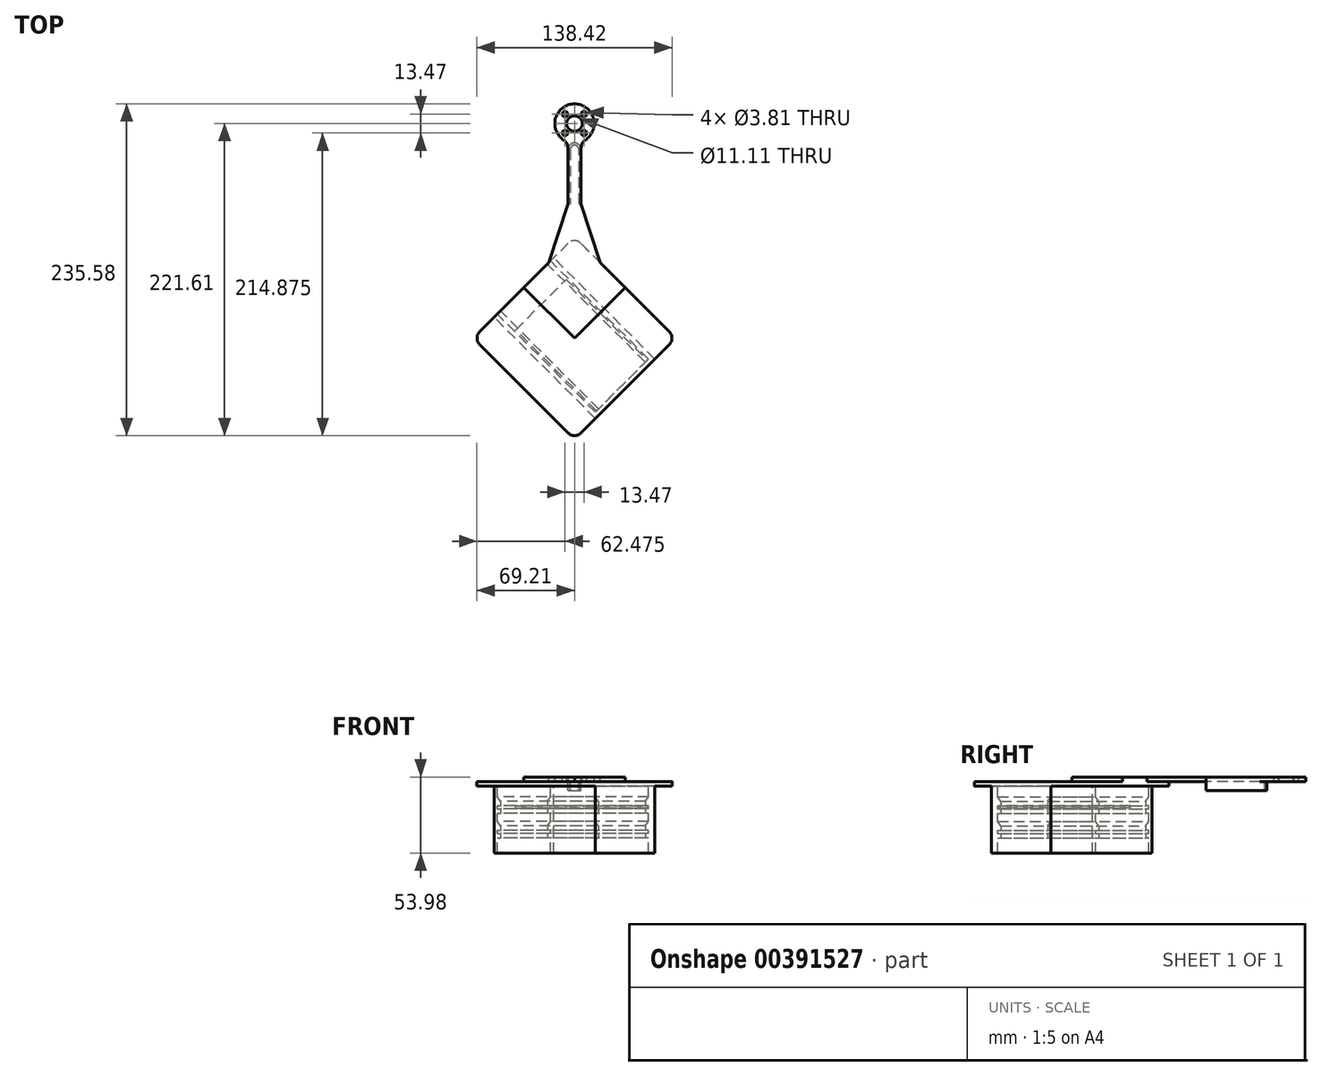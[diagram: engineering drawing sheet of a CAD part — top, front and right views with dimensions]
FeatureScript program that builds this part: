
annotation { "Feature Type Name" : "Feature", "Feature Type Description" : "" }
export const myFeature = defineFeature(function(context is Context, id is Id, definition is map)
    precondition{}
    {
        {
            var Q0;
            Q0=qCreatedBy(makeId("Top.planeOp"),FACE);
            var sketch = newSketch(context, id + "F0", { "sketchPlane" : qUnion([Q0])});
            skArc(sketch, "E0", {"start": v(4.76, 139.27) * mm, "mid": v(0, 166.37) * mm, "end": v(-4.76, 139.27) * mm});
            skCircle(sketch, "E1", {"center": v(0, 152.4) * mm, "radius": 8.06 * mm, "construction": true});
            skCircle(sketch, "E2", {"center": v(0, 152.4) * mm, "radius": 5.56 * mm});
            skCircle(sketch, "E3", {"center": v(0, 152.4) * mm, "radius": 9.53 * mm, "construction": true});
            skLineSegment(sketch, "E4", {"start": v(0, 152.4) * mm, "end": v(-9.52, 152.4) * mm, "construction": true});
            skLineSegment(sketch, "E5", {"start": v(0, 152.4) * mm, "end": v(-6.74, 159.14) * mm, "construction": true});
            skCircle(sketch, "E6", {"center": v(-6.74, 159.14) * mm, "radius": 1.9 * mm});
            skLineSegment(sketch, "E7", {"start": v(0, 152.4) * mm, "end": v(6.74, 159.14) * mm, "construction": true});
            skCircle(sketch, "E8", {"center": v(6.74, 159.14) * mm, "radius": 1.9 * mm});
            skCircle(sketch, "E9", {"center": v(6.74, 145.66) * mm, "radius": 1.9 * mm});
            skCircle(sketch, "E10", {"center": v(-6.74, 145.66) * mm, "radius": 1.9 * mm});
            skLineSegment(sketch, "E11.top", {"start": v(-18.32, 53.52) * mm, "end": v(-35.92, 35.92) * mm});
            skLineSegment(sketch, "E11.left", {"start": v(35.92, 35.92) * mm, "end": v(18.32, 53.52) * mm});
            skPoint(sketch, "E11.middle", {"position": v(0, 0) * mm});
            skLineSegment(sketch, "E12", {"start": v(0, 152.4) * mm, "end": v(0, 71.84) * mm, "construction": true});
            skLineSegment(sketch, "E13", {"start": v(-4.76, 139.27) * mm, "end": v(-4.76, 95.25) * mm});
            skLineSegment(sketch, "E14", {"start": v(-4.76, 95.25) * mm, "end": v(-18.32, 53.52) * mm});
            skLineSegment(sketch, "E15.MirrorCS", {"start": v(4.76, 95.25) * mm, "end": v(18.32, 53.52) * mm});
            skLineSegment(sketch, "E16.MirrorCS", {"start": v(4.76, 139.27) * mm, "end": v(4.76, 95.25) * mm});
            skLineSegment(sketch, "E17", {"start": v(0, 0) * mm, "end": v(-35.92, 35.92) * mm});
            skLineSegment(sketch, "E18", {"start": v(0, 0) * mm, "end": v(35.92, 35.92) * mm});
            skLineSegment(sketch, "E19", {"start": v(0, -71.84) * mm, "end": v(-71.84, 0) * mm, "construction": true});
            skLineSegment(sketch, "E20", {"start": v(-71.84, 0) * mm, "end": v(0, 71.84) * mm, "construction": true});
            skLineSegment(sketch, "E21", {"start": v(0, 71.84) * mm, "end": v(71.84, 0) * mm, "construction": true});
            skLineSegment(sketch, "E22", {"start": v(71.84, 0) * mm, "end": v(0, -71.84) * mm, "construction": true});
            skLineSegment(sketch, "E23", {"start": v(-35.92, -35.92) * mm, "end": v(35.92, 35.92) * mm, "construction": true});
            skLineSegment(sketch, "E24", {"start": v(35.92, -35.92) * mm, "end": v(-35.92, 35.92) * mm, "construction": true});
            skSolve(sketch);
        }
        {
            var Q0;
            Q0 = qSketchRegion(id + "F0", true);
            extrude(context, id + "F1", {"entities" : qUnion([Q0]), "oppositeDirection" : true, "depth" : 3.17 * mm});
        }
        {
            var Q0;
            Q0=makeQuery(id+"F1.opExtrude","CAP_FACE",FACE,{"disambiguationData":[OSD([sQuery(id+"F0.wireOp",EDGE,"E0"),sQuery(id+"F0.wireOp",EDGE,"E2"),sQuery(id+"F0.wireOp",EDGE,"E6"),sQuery(id+"F0.wireOp",EDGE,"E8"),sQuery(id+"F0.wireOp",EDGE,"E9"),sQuery(id+"F0.wireOp",EDGE,"E10"),sQuery(id+"F0.wireOp",EDGE,"E11.bottom"),sQuery(id+"F0.wireOp",EDGE,"E11.top"),sQuery(id+"F0.wireOp",EDGE,"E11.left"),sQuery(id+"F0.wireOp",EDGE,"E11.right"),sQuery(id+"F0.wireOp",EDGE,"E13"),sQuery(id+"F0.wireOp",EDGE,"E14"),sQuery(id+"F0.wireOp",EDGE,"E15.MirrorCS"),sQuery(id+"F0.wireOp",EDGE,"E16.MirrorCS"),sQuery(id+"F0.wireOp",EDGE,"a6862504-0e44-4ac9-902f-c619737a087e.1.1"),sQuery(id+"F0.wireOp",EDGE,"a6862504-0e44-4ac9-902f-c619737a087e.1.3"),sQuery(id+"F0.wireOp",EDGE,"a6862504-0e44-4ac9-902f-c619737a087e.1.4"),sQuery(id+"F0.wireOp",EDGE,"a6862504-0e44-4ac9-902f-c619737a087e.1.5"),sQuery(id+"F0.wireOp",EDGE,"a6862504-0e44-4ac9-902f-c619737a087e.1.7"),sQuery(id+"F0.wireOp",EDGE,"a6862504-0e44-4ac9-902f-c619737a087e.1.9"),sQuery(id+"F0.wireOp",EDGE,"a6862504-0e44-4ac9-902f-c619737a087e.1.11"),sQuery(id+"F0.wireOp",EDGE,"a6862504-0e44-4ac9-902f-c619737a087e.1.12"),sQuery(id+"F0.wireOp",EDGE,"a6862504-0e44-4ac9-902f-c619737a087e.1.13"),sQuery(id+"F0.wireOp",EDGE,"a6862504-0e44-4ac9-902f-c619737a087e.1.14"),sQuery(id+"F0.wireOp",EDGE,"a6862504-0e44-4ac9-902f-c619737a087e.2.1"),sQuery(id+"F0.wireOp",EDGE,"a6862504-0e44-4ac9-902f-c619737a087e.2.3"),sQuery(id+"F0.wireOp",EDGE,"a6862504-0e44-4ac9-902f-c619737a087e.2.4"),sQuery(id+"F0.wireOp",EDGE,"a6862504-0e44-4ac9-902f-c619737a087e.2.5"),sQuery(id+"F0.wireOp",EDGE,"a6862504-0e44-4ac9-902f-c619737a087e.2.7"),sQuery(id+"F0.wireOp",EDGE,"a6862504-0e44-4ac9-902f-c619737a087e.2.9"),sQuery(id+"F0.wireOp",EDGE,"a6862504-0e44-4ac9-902f-c619737a087e.2.11"),sQuery(id+"F0.wireOp",EDGE,"a6862504-0e44-4ac9-902f-c619737a087e.2.12"),sQuery(id+"F0.wireOp",EDGE,"a6862504-0e44-4ac9-902f-c619737a087e.2.13"),sQuery(id+"F0.wireOp",EDGE,"a6862504-0e44-4ac9-902f-c619737a087e.2.14"),sQuery(id+"F0.wireOp",EDGE,"a6862504-0e44-4ac9-902f-c619737a087e.3.1"),sQuery(id+"F0.wireOp",EDGE,"a6862504-0e44-4ac9-902f-c619737a087e.3.3"),sQuery(id+"F0.wireOp",EDGE,"a6862504-0e44-4ac9-902f-c619737a087e.3.4"),sQuery(id+"F0.wireOp",EDGE,"a6862504-0e44-4ac9-902f-c619737a087e.3.5"),sQuery(id+"F0.wireOp",EDGE,"a6862504-0e44-4ac9-902f-c619737a087e.3.7"),sQuery(id+"F0.wireOp",EDGE,"a6862504-0e44-4ac9-902f-c619737a087e.3.9"),sQuery(id+"F0.wireOp",EDGE,"a6862504-0e44-4ac9-902f-c619737a087e.3.11"),sQuery(id+"F0.wireOp",EDGE,"a6862504-0e44-4ac9-902f-c619737a087e.3.12"),sQuery(id+"F0.wireOp",EDGE,"a6862504-0e44-4ac9-902f-c619737a087e.3.13"),sQuery(id+"F0.wireOp",EDGE,"a6862504-0e44-4ac9-902f-c619737a087e.3.14")])],"isStart":false});
            var sketch = newSketch(context, id + "F2", { "sketchPlane" : qUnion([Q0])});
            skLineSegment(sketch, "E25", {"start": v(14.82, 57.02) * mm, "end": v(-57.02, -14.82) * mm});
            skLineSegment(sketch, "E26", {"start": v(-57.02, -14.82) * mm, "end": v(-54.78, -17.06) * mm});
            skLineSegment(sketch, "E27", {"start": v(-54.78, -17.06) * mm, "end": v(14.82, 52.53) * mm});
            skLineSegment(sketch, "E28", {"start": v(17.06, 54.78) * mm, "end": v(14.82, 57.02) * mm});
            skLineSegment(sketch, "E29", {"start": v(0, 0) * mm, "end": v(-35.92, 35.92) * mm, "construction": true});
            skLineSegment(sketch, "E30", {"start": v(0, 0) * mm, "end": v(35.92, 35.92) * mm, "construction": true});
            skLineSegment(sketch, "E31", {"start": v(35.92, 35.92) * mm, "end": v(-35.92, -35.92) * mm, "construction": true});
            skLineSegment(sketch, "E32.MirrorCS", {"start": v(54.78, 17.06) * mm, "end": v(57.02, 14.82) * mm});
            skLineSegment(sketch, "E33.MirrorCS", {"start": v(-14.82, -57.02) * mm, "end": v(-17.06, -54.78) * mm});
            skLineSegment(sketch, "E34.MirrorCS", {"start": v(57.02, 14.82) * mm, "end": v(-14.82, -57.02) * mm});
            skLineSegment(sketch, "E35.MirrorCS", {"start": v(-17.06, -54.78) * mm, "end": v(52.53, 14.82) * mm});
            skLineSegment(sketch, "E36", {"start": v(17.06, 54.78) * mm, "end": v(54.78, 17.06) * mm});
            skLineSegment(sketch, "E37", {"start": v(14.82, 52.53) * mm, "end": v(52.53, 14.82) * mm});
            skSolve(sketch);
        }
        {
            var Q0;
            Q0 = qSketchRegion(id + "F2", true);
            extrude(context, id + "F3", {"entities" : qUnion([Q0]), "depth" : 50.8 * mm});
        }
        {
            var Q0;
            Q0=makeQuery(id+"F3.opExtrude","SWEPT_FACE",FACE,{"disambiguationData":[OSD([sQuery(id+"F2.wireOp",EDGE,"E33.MirrorCS")])]});
            var sketch = newSketch(context, id + "F4", { "sketchPlane" : qUnion([Q0])});
            skLineSegment(sketch, "E38.top", {"start": v(-26.67, -20.32) * mm, "end": v(-23.5, -20.32) * mm});
            skLineSegment(sketch, "E38.left", {"start": v(-26.67, -19.05) * mm, "end": v(-26.67, -20.32) * mm});
            skLineSegment(sketch, "E38.right", {"start": v(-23.5, -17.14) * mm, "end": v(-23.5, -20.32) * mm});
            skLineSegment(sketch, "E39.bottom", {"start": v(-26.67, -22.48) * mm, "end": v(-23.5, -22.48) * mm});
            skLineSegment(sketch, "E39.top", {"start": v(-26.67, -25.65) * mm, "end": v(-23.5, -25.65) * mm});
            skLineSegment(sketch, "E39.left", {"start": v(-26.67, -22.48) * mm, "end": v(-26.67, -25.65) * mm});
            skLineSegment(sketch, "E39.right", {"start": v(-23.5, -22.48) * mm, "end": v(-23.5, -25.65) * mm});
            skLineSegment(sketch, "E40", {"start": v(0, 0) * mm, "end": v(0, -54) * mm, "construction": true});
            skLineSegment(sketch, "E41.MirrorCS", {"start": v(26.67, -22.48) * mm, "end": v(26.67, -25.65) * mm});
            skLineSegment(sketch, "E42.MirrorCS", {"start": v(26.67, -25.65) * mm, "end": v(23.5, -25.65) * mm});
            skLineSegment(sketch, "E43.MirrorCS", {"start": v(26.67, -22.48) * mm, "end": v(23.5, -22.48) * mm});
            skLineSegment(sketch, "E44.MirrorCS", {"start": v(23.5, -22.48) * mm, "end": v(23.5, -25.65) * mm});
            skLineSegment(sketch, "E45.MirrorCS", {"start": v(23.5, -17.14) * mm, "end": v(23.5, -20.32) * mm});
            skLineSegment(sketch, "E46.MirrorCS", {"start": v(26.67, -20.32) * mm, "end": v(23.5, -20.32) * mm});
            skLineSegment(sketch, "E47.MirrorCS", {"start": v(26.67, -19.05) * mm, "end": v(26.67, -20.32) * mm});
            skLineSegment(sketch, "E48", {"start": v(-23.5, -17.15) * mm, "end": v(-26.67, -13.97) * mm});
            skLineSegment(sketch, "E49", {"start": v(23.5, -17.15) * mm, "end": v(26.67, -13.97) * mm});
            skLineSegment(sketch, "E50", {"start": v(-26.67, -13.97) * mm, "end": v(-26.67, -19.05) * mm});
            skLineSegment(sketch, "E51", {"start": v(26.67, -13.97) * mm, "end": v(26.67, -19.05) * mm});
            skLineSegment(sketch, "E52.0.1.0", {"start": v(-26.67, -39.94) * mm, "end": v(-23.5, -39.94) * mm});
            skLineSegment(sketch, "E52.0.1.1", {"start": v(-26.67, -36.51) * mm, "end": v(-26.67, -37.78) * mm});
            skLineSegment(sketch, "E52.0.1.2", {"start": v(-26.67, -37.78) * mm, "end": v(-23.5, -37.78) * mm});
            skLineSegment(sketch, "E52.0.1.3", {"start": v(-23.5, -34.6) * mm, "end": v(-23.5, -37.78) * mm});
            skLineSegment(sketch, "E52.0.1.4", {"start": v(-23.5, -34.6) * mm, "end": v(-26.67, -31.43) * mm});
            skLineSegment(sketch, "E52.0.1.5", {"start": v(26.67, -36.51) * mm, "end": v(26.67, -37.78) * mm});
            skLineSegment(sketch, "E52.0.1.6", {"start": v(-26.67, -43.12) * mm, "end": v(-23.5, -43.12) * mm});
            skLineSegment(sketch, "E52.0.1.7", {"start": v(-26.67, -39.94) * mm, "end": v(-26.67, -43.12) * mm});
            skLineSegment(sketch, "E52.0.1.8", {"start": v(26.67, -31.43) * mm, "end": v(26.67, -36.51) * mm});
            skLineSegment(sketch, "E52.0.1.9", {"start": v(23.5, -34.6) * mm, "end": v(26.67, -31.43) * mm});
            skLineSegment(sketch, "E52.0.1.10", {"start": v(26.67, -37.78) * mm, "end": v(23.5, -37.78) * mm});
            skLineSegment(sketch, "E52.0.1.11", {"start": v(-23.5, -39.94) * mm, "end": v(-23.5, -43.12) * mm});
            skLineSegment(sketch, "E52.0.1.12", {"start": v(26.67, -39.94) * mm, "end": v(26.67, -43.12) * mm});
            skLineSegment(sketch, "E52.0.1.13", {"start": v(26.67, -43.12) * mm, "end": v(23.5, -43.12) * mm});
            skLineSegment(sketch, "E52.0.1.14", {"start": v(26.67, -39.94) * mm, "end": v(23.5, -39.94) * mm});
            skLineSegment(sketch, "E52.0.1.15", {"start": v(23.5, -39.94) * mm, "end": v(23.5, -43.12) * mm});
            skLineSegment(sketch, "E52.0.1.16", {"start": v(23.5, -34.6) * mm, "end": v(23.5, -37.78) * mm});
            skLineSegment(sketch, "E52.0.1.17", {"start": v(-26.67, -31.43) * mm, "end": v(-26.67, -36.51) * mm});
            skLineSegment(sketch, "E52.direction1", {"start": v(-26.67, -25.65) * mm, "end": v(-1.27, -25.65) * mm, "construction": true});
            skLineSegment(sketch, "E52.direction2", {"start": v(-26.67, -25.65) * mm, "end": v(-26.67, -43.12) * mm, "construction": true});
            skSolve(sketch);
        }
        {
            var Q0;
            Q0 = qSketchRegion(id + "F4", true);
            var Q1;
            Q1=makeQuery(id+"F3.opExtrude","SWEPT_FACE",FACE,{"disambiguationData":[OSD([sQuery(id+"F2.wireOp",EDGE,"E37")])]});
            extrude(context, id + "F5", {"entities" : qUnion([Q0]), "operationType" : NewBodyOperationType.ADD, "endBound" : BoundingType.UP_TO_SURFACE, "oppositeDirection" : true, "endBoundEntityFace" : qUnion([Q1]), "depth" : 25.4 * mm});
        }
        {
            var Q0;
            Q0=makeQuery(id+"F5.opExtrude","SWEPT_FACE",FACE,{"disambiguationData":[OSD([sQuery(id+"F4.wireOp",EDGE,"E38.top")])]});
            var sketch = newSketch(context, id + "F6", { "sketchPlane" : qUnion([Q0])});
            skLineSegment(sketch, "E53", {"start": v(15.72, 51.64) * mm, "end": v(-41.76, -5.84) * mm});
            skLineSegment(sketch, "E54", {"start": v(-41.76, -5.84) * mm, "end": v(-5.84, -41.76) * mm});
            skLineSegment(sketch, "E55", {"start": v(-5.84, -41.76) * mm, "end": v(51.64, 15.72) * mm});
            skLineSegment(sketch, "E56", {"start": v(51.64, 15.72) * mm, "end": v(15.72, 51.64) * mm});
            skLineSegment(sketch, "E57", {"start": v(33.68, 33.68) * mm, "end": v(-23.8, -23.8) * mm, "construction": true});
            skLineSegment(sketch, "E58", {"start": v(-13.02, 22.9) * mm, "end": v(22.9, -13.02) * mm, "construction": true});
            skPoint(sketch, "E59", {"position": v(4.94, 4.94) * mm});
            skLineSegment(sketch, "E60", {"start": v(0, 0) * mm, "end": v(90.54, 90.54) * mm, "construction": true});
            skSolve(sketch);
        }
        {
            var Q0;
            Q0 = qSketchRegion(id + "F6", true);
            extrude(context, id + "F7", {"entities" : qUnion([Q0]), "depth" : 1.78 * mm});
        }
        {
            var Q0;
            Q0=makeQuery(id+"F1.opExtrude","CAP_FACE",FACE,{"disambiguationData":[OSD([sQuery(id+"F0.wireOp",EDGE,"E0"),sQuery(id+"F0.wireOp",EDGE,"E2"),sQuery(id+"F0.wireOp",EDGE,"E6"),sQuery(id+"F0.wireOp",EDGE,"E8"),sQuery(id+"F0.wireOp",EDGE,"E9"),sQuery(id+"F0.wireOp",EDGE,"E10"),sQuery(id+"F0.wireOp",EDGE,"E11.bottom"),sQuery(id+"F0.wireOp",EDGE,"E11.top"),sQuery(id+"F0.wireOp",EDGE,"E11.left"),sQuery(id+"F0.wireOp",EDGE,"E11.right"),sQuery(id+"F0.wireOp",EDGE,"E13"),sQuery(id+"F0.wireOp",EDGE,"E14"),sQuery(id+"F0.wireOp",EDGE,"E15.MirrorCS"),sQuery(id+"F0.wireOp",EDGE,"E16.MirrorCS"),sQuery(id+"F0.wireOp",EDGE,"a6862504-0e44-4ac9-902f-c619737a087e.1.1"),sQuery(id+"F0.wireOp",EDGE,"a6862504-0e44-4ac9-902f-c619737a087e.1.3"),sQuery(id+"F0.wireOp",EDGE,"a6862504-0e44-4ac9-902f-c619737a087e.1.4"),sQuery(id+"F0.wireOp",EDGE,"a6862504-0e44-4ac9-902f-c619737a087e.1.5"),sQuery(id+"F0.wireOp",EDGE,"a6862504-0e44-4ac9-902f-c619737a087e.1.7"),sQuery(id+"F0.wireOp",EDGE,"a6862504-0e44-4ac9-902f-c619737a087e.1.9"),sQuery(id+"F0.wireOp",EDGE,"a6862504-0e44-4ac9-902f-c619737a087e.1.11"),sQuery(id+"F0.wireOp",EDGE,"a6862504-0e44-4ac9-902f-c619737a087e.1.12"),sQuery(id+"F0.wireOp",EDGE,"a6862504-0e44-4ac9-902f-c619737a087e.1.13"),sQuery(id+"F0.wireOp",EDGE,"a6862504-0e44-4ac9-902f-c619737a087e.1.14"),sQuery(id+"F0.wireOp",EDGE,"a6862504-0e44-4ac9-902f-c619737a087e.2.1"),sQuery(id+"F0.wireOp",EDGE,"a6862504-0e44-4ac9-902f-c619737a087e.2.3"),sQuery(id+"F0.wireOp",EDGE,"a6862504-0e44-4ac9-902f-c619737a087e.2.4"),sQuery(id+"F0.wireOp",EDGE,"a6862504-0e44-4ac9-902f-c619737a087e.2.5"),sQuery(id+"F0.wireOp",EDGE,"a6862504-0e44-4ac9-902f-c619737a087e.2.7"),sQuery(id+"F0.wireOp",EDGE,"a6862504-0e44-4ac9-902f-c619737a087e.2.9"),sQuery(id+"F0.wireOp",EDGE,"a6862504-0e44-4ac9-902f-c619737a087e.2.11"),sQuery(id+"F0.wireOp",EDGE,"a6862504-0e44-4ac9-902f-c619737a087e.2.12"),sQuery(id+"F0.wireOp",EDGE,"a6862504-0e44-4ac9-902f-c619737a087e.2.13"),sQuery(id+"F0.wireOp",EDGE,"a6862504-0e44-4ac9-902f-c619737a087e.2.14"),sQuery(id+"F0.wireOp",EDGE,"a6862504-0e44-4ac9-902f-c619737a087e.3.1"),sQuery(id+"F0.wireOp",EDGE,"a6862504-0e44-4ac9-902f-c619737a087e.3.3"),sQuery(id+"F0.wireOp",EDGE,"a6862504-0e44-4ac9-902f-c619737a087e.3.4"),sQuery(id+"F0.wireOp",EDGE,"a6862504-0e44-4ac9-902f-c619737a087e.3.5"),sQuery(id+"F0.wireOp",EDGE,"a6862504-0e44-4ac9-902f-c619737a087e.3.7"),sQuery(id+"F0.wireOp",EDGE,"a6862504-0e44-4ac9-902f-c619737a087e.3.9"),sQuery(id+"F0.wireOp",EDGE,"a6862504-0e44-4ac9-902f-c619737a087e.3.11"),sQuery(id+"F0.wireOp",EDGE,"a6862504-0e44-4ac9-902f-c619737a087e.3.12"),sQuery(id+"F0.wireOp",EDGE,"a6862504-0e44-4ac9-902f-c619737a087e.3.13"),sQuery(id+"F0.wireOp",EDGE,"a6862504-0e44-4ac9-902f-c619737a087e.3.14")])],"isStart":false});
            var sketch = newSketch(context, id + "F8", { "sketchPlane" : qUnion([Q0])});
            skLineSegment(sketch, "E61", {"start": v(0, 71.84) * mm, "end": v(71.84, 0) * mm});
            skLineSegment(sketch, "E62", {"start": v(71.84, 0) * mm, "end": v(0, -71.84) * mm});
            skLineSegment(sketch, "E63", {"start": v(0, -71.84) * mm, "end": v(-71.84, 0) * mm});
            skLineSegment(sketch, "E64", {"start": v(-71.84, 0) * mm, "end": v(0, 71.84) * mm});
            skLineSegment(sketch, "E65", {"start": v(-35.92, -35.92) * mm, "end": v(35.92, 35.92) * mm, "construction": true});
            skLineSegment(sketch, "E66", {"start": v(-35.92, 35.92) * mm, "end": v(35.92, -35.92) * mm, "construction": true});
            skPoint(sketch, "E67", {"position": v(0, 0) * mm});
            skSolve(sketch);
        }
        {
            var Q0;
            Q0 = qSketchRegion(id + "F8", true);
            extrude(context, id + "F9", {"entities" : qUnion([Q0]), "operationType" : NewBodyOperationType.ADD, "depth" : 3.17 * mm});
        }
        {
            var Q0;
            Q0=makeQuery(id+"F1.opExtrude","SWEPT_EDGE",EDGE,{"disambiguationData":[OSD([sQuery(id+"F0.wireOp",EDGE,"E0"),sQuery(id+"F0.wireOp",EDGE,"E13")])]});
            var Q1;
            Q1=makeQuery(id+"F1.opExtrude","SWEPT_EDGE",EDGE,{"disambiguationData":[OSD([sQuery(id+"F0.wireOp",EDGE,"E0"),sQuery(id+"F0.wireOp",EDGE,"E16.MirrorCS")])]});
            fillet(context, id + "F10", {"entities" : qUnion([Q0, Q1]), "radius" : 6.35 * mm, "tangentPropagation" : true, "allowEdgeOverflow" : false});
        }
        {
            var Q0;
            Q0=makeQuery(id+"F1.opExtrude","CAP_FACE",FACE,{"disambiguationData":[OSD([sQuery(id+"F0.wireOp",EDGE,"E0"),sQuery(id+"F0.wireOp",EDGE,"E2"),sQuery(id+"F0.wireOp",EDGE,"E6"),sQuery(id+"F0.wireOp",EDGE,"E8"),sQuery(id+"F0.wireOp",EDGE,"E9"),sQuery(id+"F0.wireOp",EDGE,"E10"),sQuery(id+"F0.wireOp",EDGE,"E11.top"),sQuery(id+"F0.wireOp",EDGE,"E11.left"),sQuery(id+"F0.wireOp",EDGE,"E13"),sQuery(id+"F0.wireOp",EDGE,"E14"),sQuery(id+"F0.wireOp",EDGE,"E15.MirrorCS"),sQuery(id+"F0.wireOp",EDGE,"E16.MirrorCS"),sQuery(id+"F0.wireOp",EDGE,"E17"),sQuery(id+"F0.wireOp",EDGE,"E18")])],"isStart":false});
            var sketch = newSketch(context, id + "F11", { "sketchPlane" : qUnion([Q0])});
            skLineSegment(sketch, "E68", {"start": v(-4.76, -95.25) * mm, "end": v(-4.76, -135.39) * mm});
            skLineSegment(sketch, "E69", {"start": v(-4.76, -135.39) * mm, "end": v(-3.03, -137.33) * mm});
            skLineSegment(sketch, "E70", {"start": v(3.03, -137.33) * mm, "end": v(4.76, -135.39) * mm});
            skLineSegment(sketch, "E71", {"start": v(4.76, -135.39) * mm, "end": v(4.76, -95.25) * mm});
            skLineSegment(sketch, "E72", {"start": v(4.76, -95.25) * mm, "end": v(3.17, -95.25) * mm});
            skLineSegment(sketch, "E73", {"start": v(3.17, -95.25) * mm, "end": v(3.17, -134.78) * mm});
            skLineSegment(sketch, "E74", {"start": v(3.17, -134.78) * mm, "end": v(1.9, -136.21) * mm});
            skLineSegment(sketch, "E75", {"start": v(-1.9, -136.21) * mm, "end": v(-3.17, -134.78) * mm});
            skLineSegment(sketch, "E76", {"start": v(-3.17, -134.78) * mm, "end": v(-3.17, -95.25) * mm});
            skLineSegment(sketch, "E77", {"start": v(-3.17, -95.25) * mm, "end": v(-4.76, -95.25) * mm});
            skPoint(sketch, "E78.visualSharp", {"position": v(0, -138.32) * mm});
            skArc(sketch, "E78.filletArc", {"start": v(-1.9, -136.21) * mm, "mid": v(0, -137.06) * mm, "end": v(1.9, -136.21) * mm});
            skPoint(sketch, "E79.visualSharp", {"position": v(0, -140.7) * mm});
            skArc(sketch, "E79.filletArc", {"start": v(-3.03, -137.33) * mm, "mid": v(0, -138.68) * mm, "end": v(3.03, -137.33) * mm});
            skSolve(sketch);
        }
        {
            var Q0;
            Q0 = qSketchRegion(id + "F11", true);
            extrude(context, id + "F12", {"entities" : qUnion([Q0]), "operationType" : NewBodyOperationType.ADD, "depth" : 6.35 * mm});
        }
        {
            var Q0;
            Q0=makeQuery(id+"F12.opExtrude","SWEPT_EDGE",EDGE,{"disambiguationData":[OSD([sQuery(id+"F0.wireOp",EDGE,"E0"),sQuery(id+"F0.wireOp",EDGE,"E2"),sQuery(id+"F0.wireOp",EDGE,"E6"),sQuery(id+"F0.wireOp",EDGE,"E8"),sQuery(id+"F0.wireOp",EDGE,"E9"),sQuery(id+"F0.wireOp",EDGE,"E10"),sQuery(id+"F0.wireOp",EDGE,"E11.top"),sQuery(id+"F0.wireOp",EDGE,"E11.left"),sQuery(id+"F0.wireOp",EDGE,"E13"),sQuery(id+"F0.wireOp",EDGE,"E14"),sQuery(id+"F0.wireOp",EDGE,"E15.MirrorCS"),sQuery(id+"F0.wireOp",EDGE,"E16.MirrorCS"),sQuery(id+"F0.wireOp",EDGE,"E17"),sQuery(id+"F0.wireOp",EDGE,"E18"),sQuery(id+"F11.wireOp",EDGE,"E68"),sQuery(id+"F11.wireOp",EDGE,"E69")])]});
            var Q1;
            Q1=makeQuery(id+"F12.opExtrude","SWEPT_EDGE",EDGE,{"disambiguationData":[OSD([sQuery(id+"F0.wireOp",EDGE,"E0"),sQuery(id+"F0.wireOp",EDGE,"E2"),sQuery(id+"F0.wireOp",EDGE,"E6"),sQuery(id+"F0.wireOp",EDGE,"E8"),sQuery(id+"F0.wireOp",EDGE,"E9"),sQuery(id+"F0.wireOp",EDGE,"E10"),sQuery(id+"F0.wireOp",EDGE,"E11.top"),sQuery(id+"F0.wireOp",EDGE,"E11.left"),sQuery(id+"F0.wireOp",EDGE,"E13"),sQuery(id+"F0.wireOp",EDGE,"E14"),sQuery(id+"F0.wireOp",EDGE,"E15.MirrorCS"),sQuery(id+"F0.wireOp",EDGE,"E16.MirrorCS"),sQuery(id+"F0.wireOp",EDGE,"E17"),sQuery(id+"F0.wireOp",EDGE,"E18"),sQuery(id+"F11.wireOp",EDGE,"E70"),sQuery(id+"F11.wireOp",EDGE,"E71")])]});
            fillet(context, id + "F13", {"entities" : qUnion([Q0, Q1]), "radius" : 5.08 * mm, "tangentPropagation" : true, "allowEdgeOverflow" : false});
        }
        {
            var Q0;
            Q0=makeQuery(id+"F12.opExtrude","SWEPT_EDGE",EDGE,{"disambiguationData":[OSD([sQuery(id+"F11.wireOp",EDGE,"E73"),sQuery(id+"F11.wireOp",EDGE,"E74")])]});
            var Q1;
            Q1=makeQuery(id+"F12.opExtrude","SWEPT_EDGE",EDGE,{"disambiguationData":[OSD([sQuery(id+"F11.wireOp",EDGE,"E75"),sQuery(id+"F11.wireOp",EDGE,"E76")])]});
            fillet(context, id + "F14", {"entities" : qUnion([Q0, Q1]), "radius" : 2.54 * mm, "tangentPropagation" : true, "allowEdgeOverflow" : false});
        }
        {
            var Q0;
            Q0=makeQuery(id+"F9.opExtrude","SWEPT_EDGE",EDGE,{"disambiguationData":[OSD([sQuery(id+"F8.wireOp",EDGE,"E62"),sQuery(id+"F8.wireOp",EDGE,"E63")])]});
            var Q1;
            Q1=makeQuery(id+"F9.opExtrude","SWEPT_EDGE",EDGE,{"disambiguationData":[OSD([sQuery(id+"F8.wireOp",EDGE,"E63"),sQuery(id+"F8.wireOp",EDGE,"E64")])]});
            var Q2;
            Q2=makeQuery(id+"F9.opExtrude","SWEPT_EDGE",EDGE,{"disambiguationData":[OSD([sQuery(id+"F8.wireOp",EDGE,"E61"),sQuery(id+"F8.wireOp",EDGE,"E64")])]});
            var Q3;
            Q3=makeQuery(id+"F9.opExtrude","SWEPT_EDGE",EDGE,{"disambiguationData":[OSD([sQuery(id+"F8.wireOp",EDGE,"E61"),sQuery(id+"F8.wireOp",EDGE,"E62")])]});
            fillet(context, id + "F15", {"entities" : qUnion([Q0, Q1, Q2, Q3]), "radius" : 6.35 * mm, "tangentPropagation" : true, "allowEdgeOverflow" : false});
        }
    });
